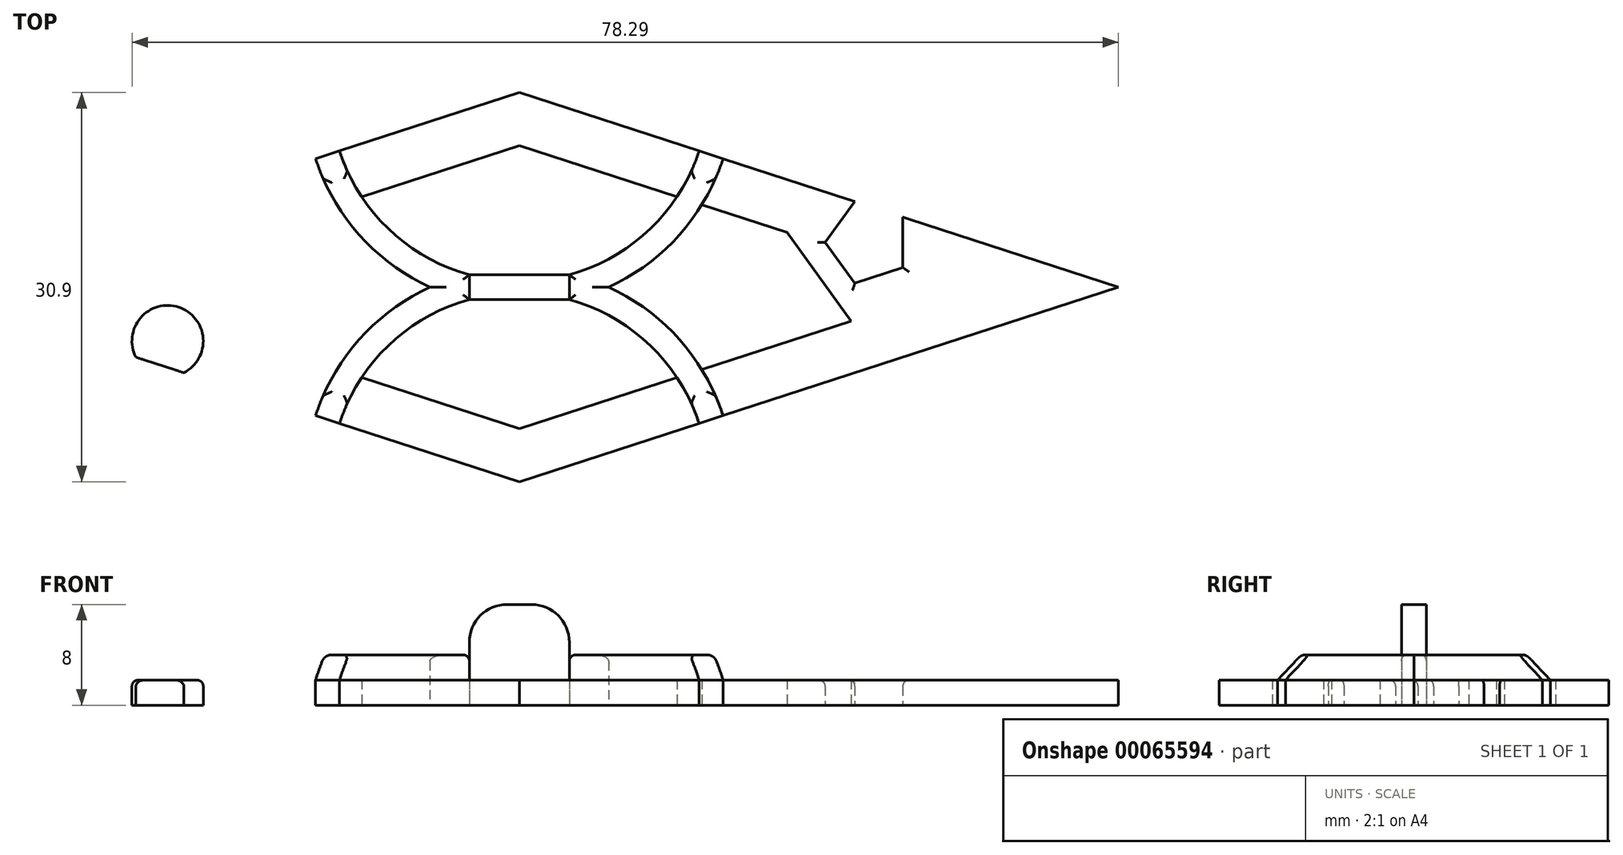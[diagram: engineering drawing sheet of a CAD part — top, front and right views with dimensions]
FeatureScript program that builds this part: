
annotation { "Feature Type Name" : "Feature", "Feature Type Description" : "" }
export const myFeature = defineFeature(function(context is Context, id is Id, definition is map)
    precondition{}
    {
        {
            var Q0;
            Q0=qCreatedBy(makeId("Top.planeOp"),FACE);
            var sketch = newSketch(context, id + "F0", { "sketchPlane" : qUnion([Q0])});
            skLineSegment(sketch, "E0", {"start": v(-47.55, 0) * mm, "end": v(0, -15.45) * mm});
            skLineSegment(sketch, "E1", {"start": v(-28.53, -6.18) * mm, "end": v(-27.91, -4.28) * mm});
            skArc(sketch, "E2", {"start": v(-30.43, -5.56) * mm, "mid": v(-27.04, -1.59) * mm, "end": v(-26.63, -6.8) * mm});
            skLineSegment(sketch, "E3.MirrorCS", {"start": v(47.55, 0) * mm, "end": v(0, -15.45) * mm});
            skLineSegment(sketch, "E4.MirrorCS", {"start": v(28.53, -6.18) * mm, "end": v(29.15, -8.08) * mm});
            skArc(sketch, "E5.MirrorCS", {"start": v(30.43, -5.56) * mm, "mid": v(30.02, -10.77) * mm, "end": v(26.63, -6.8) * mm});
            skLineSegment(sketch, "E6", {"start": v(-47.55, 0) * mm, "end": v(0, 15.45) * mm});
            skCircle(sketch, "E7.cCircle", {"center": v(-29.38, 8.8) * mm, "radius": 3.4 * mm, "construction": true});
            skLineSegment(sketch, "E7.0", {"start": v(-26.63, 6.8) * mm, "end": v(-30.43, 5.56) * mm});
            skLineSegment(sketch, "E7.1", {"start": v(-30.43, 5.56) * mm, "end": v(-32.78, 8.8) * mm});
            skLineSegment(sketch, "E7.2", {"start": v(-32.78, 8.8) * mm, "end": v(-30.43, 12.03) * mm});
            skLineSegment(sketch, "E7.3", {"start": v(-30.43, 12.03) * mm, "end": v(-26.63, 10.8) * mm});
            skLineSegment(sketch, "E7.4", {"start": v(-26.63, 10.8) * mm, "end": v(-26.63, 6.8) * mm});
            skLineSegment(sketch, "E8.MirrorCS", {"start": v(47.55, 0) * mm, "end": v(0, 15.45) * mm});
            skLineSegment(sketch, "E9.MirrorCS", {"start": v(26.63, 6.8) * mm, "end": v(30.43, 5.56) * mm});
            skLineSegment(sketch, "E10.MirrorCS", {"start": v(24.28, 3.56) * mm, "end": v(26.63, 6.8) * mm});
            skLineSegment(sketch, "E11.MirrorCS", {"start": v(26.63, 0.33) * mm, "end": v(24.28, 3.56) * mm});
            skLineSegment(sketch, "E12.MirrorCS", {"start": v(30.43, 1.56) * mm, "end": v(26.63, 0.33) * mm});
            skCircle(sketch, "E13.MirrorC", {"center": v(27.68, 3.56) * mm, "radius": 3.4 * mm, "construction": true});
            skLineSegment(sketch, "E14.MirrorCS", {"start": v(30.43, 5.56) * mm, "end": v(30.43, 1.56) * mm});
            skLineSegment(sketch, "E15.0", {"start": v(26.35, -2.68) * mm, "end": v(0, -11.25) * mm});
            skLineSegment(sketch, "E16.0", {"start": v(26.35, -2.68) * mm, "end": v(21.24, 4.34) * mm});
            skLineSegment(sketch, "E17.trimOffspring", {"start": v(21.24, 4.34) * mm, "end": v(0, 11.25) * mm});
            skLineSegment(sketch, "E18.trimOffspring", {"start": v(-22.94, -3.8) * mm, "end": v(0, -11.25) * mm});
            skLineSegment(sketch, "E19.trimOffspring", {"start": v(-27.91, 2.18) * mm, "end": v(0, 11.25) * mm});
            skArc(sketch, "E20", {"start": v(16.17, -10.2) * mm, "mid": v(0, 1.55) * mm, "end": v(-16.17, -10.2) * mm});
            skArc(sketch, "E21", {"start": v(14.27, -10.82) * mm, "mid": v(0, -0.45) * mm, "end": v(-14.27, -10.82) * mm});
            skArc(sketch, "E22.MirrorCS", {"start": v(16.17, 10.2) * mm, "mid": v(0, -1.55) * mm, "end": v(-16.17, 10.2) * mm});
            skArc(sketch, "E23.MirrorCS", {"start": v(14.27, 10.82) * mm, "mid": v(0, 0.45) * mm, "end": v(-14.27, 10.82) * mm});
            skArc(sketch, "E24", {"start": v(-22.94, -3.8) * mm, "mid": v(-24.55, -0.57) * mm, "end": v(-27.91, 0.72) * mm});
            skLineSegment(sketch, "E25.trimOffspring", {"start": v(-27.91, 0.72) * mm, "end": v(-27.91, 2.18) * mm});
            skLineSegment(sketch, "E26.rect.bottom", {"start": v(3.97, 0.99) * mm, "end": v(-3.97, 0.99) * mm});
            skLineSegment(sketch, "E26.rect.top", {"start": v(3.97, -0.99) * mm, "end": v(-3.97, -0.99) * mm});
            skLineSegment(sketch, "E26.rect.left", {"start": v(3.97, 0.99) * mm, "end": v(3.97, -0.99) * mm});
            skLineSegment(sketch, "E26.rect.right", {"start": v(-3.97, 0.99) * mm, "end": v(-3.97, -0.99) * mm});
            skPoint(sketch, "E26.rect.middle", {"position": v(0, 0) * mm});
            skSolve(sketch);
        }
        {
            var Q0;
            {var subQ13=sQuery(id+"F0.wireOp",EDGE,"E2");Q0=makeQuery(id+"F0.imprint","IMPRINT",FACE,{"disambiguationData":[TD([[makeQuery(id+"F0.imprint","IMPRINT",EDGE,{"derivedFrom":subQ13}),1.0]])]});}
            var Q1;
            {var subQ2=sQuery(id+"F0.wireOp",EDGE,"E5.MirrorCS");Q1=makeQuery(id+"F0.imprint","IMPRINT",FACE,{"disambiguationData":[TD([[makeQuery(id+"F0.imprint","IMPRINT",EDGE,{"derivedFrom":subQ2}),-1.0]])]});}
            var Q2;
            Q2=makeQuery(id+"F0.imprint","IMPRINT",FACE,{"disambiguationData":[TD([[makeQuery(id+"F0.imprint","IMPRINT",EDGE,{"derivedFrom":sQuery(id+"F0.wireOp",EDGE,"E7.0")}),-1.0]])]});
            var Q3;
            {var subQ0=sQuery(id+"F0.wireOp",EDGE,"59c43cce-ddf3-466e-a771-7dc7d053fc7f");Q3=makeQuery(id+"F0.imprint","IMPRINT",FACE,{"disambiguationData":[TD([[makeQuery(id+"F0.imprint","IMPRINT",EDGE,{"derivedFrom":subQ0}),1.0]])]});}
            var Q4;
            {var subQ6=sQuery(id+"F0.wireOp",EDGE,"E8.MirrorCS");var subQ7=sQuery(id+"F0.wireOp",EDGE,"E6");var subQ8=makeQuery(id+"F0.imprint","INTERSECT",VERTEX,{"derivedFrom":[subQ7,subQ6]});Q4=makeQuery(id+"F0.imprint","IMPRINT",FACE,{"disambiguationData":[TD([[makeQuery(id+"F0.imprint","IMPRINT",EDGE,{"disambiguationData":[TD([[subQ8,1.0]])],"derivedFrom":subQ7}),-1.0]])]});}
            var Q5;
            {var subQ1=sQuery(id+"F0.wireOp",EDGE,"E10.MirrorCS");Q5=makeQuery(id+"F0.imprint","IMPRINT",FACE,{"disambiguationData":[TD([[makeQuery(id+"F0.imprint","IMPRINT",EDGE,{"derivedFrom":subQ1}),1.0]])]});}
            var Q6;
            {var subQ5=sQuery(id+"F0.wireOp",EDGE,"E3.MirrorCS");var subQ6=sQuery(id+"F0.wireOp",EDGE,"E0");var subQ7=makeQuery(id+"F0.imprint","INTERSECT",VERTEX,{"derivedFrom":[subQ6,subQ5]});Q6=makeQuery(id+"F0.imprint","IMPRINT",FACE,{"disambiguationData":[TD([[makeQuery(id+"F0.imprint","IMPRINT",EDGE,{"disambiguationData":[TD([[subQ7,1.0]])],"derivedFrom":subQ6}),1.0]])]});}
            extrude(context, id + "F1", {"entities" : qUnion([Q0, Q1, Q2, Q3, Q4, Q5, Q6]), "depth" : 2 * mm});
        }
        {
            var Q0;
            {var subQ0=sQuery(id+"F0.wireOp",EDGE,"E20");var subQ1=sQuery(id+"F0.wireOp",EDGE,"E15.0");var subQ2=makeQuery(id+"F0.imprint","INTERSECT",VERTEX,{"derivedFrom":[subQ1,subQ0]});Q0=makeQuery(id+"F0.imprint","IMPRINT",FACE,{"disambiguationData":[TD([[makeQuery(id+"F0.imprint","IMPRINT",EDGE,{"disambiguationData":[TD([[subQ2,-1.0]])],"derivedFrom":subQ1}),-1.0]])]});}
            var Q1;
            {var subQ0=sQuery(id+"F0.wireOp",EDGE,"E20");var subQ1=sQuery(id+"F0.wireOp",EDGE,"E0");var subQ2=makeQuery(id+"F0.imprint","INTERSECT",VERTEX,{"derivedFrom":[subQ1,subQ0]});Q1=makeQuery(id+"F0.imprint","IMPRINT",FACE,{"disambiguationData":[TD([[makeQuery(id+"F0.imprint","IMPRINT",EDGE,{"disambiguationData":[TD([[subQ2,-1.0]])],"derivedFrom":subQ1}),1.0]])]});}
            var Q2;
            {var subQ0=sQuery(id+"F0.wireOp",EDGE,"E20");var subQ1=sQuery(id+"F0.wireOp",EDGE,"E3.MirrorCS");var subQ2=makeQuery(id+"F0.imprint","INTERSECT",VERTEX,{"derivedFrom":[subQ1,subQ0]});Q2=makeQuery(id+"F0.imprint","IMPRINT",FACE,{"disambiguationData":[TD([[makeQuery(id+"F0.imprint","IMPRINT",EDGE,{"disambiguationData":[TD([[subQ2,-1.0]])],"derivedFrom":subQ1}),-1.0]])]});}
            var Q3;
            {var subQ0=sQuery(id+"F0.wireOp",EDGE,"E22.MirrorCS");var subQ1=sQuery(id+"F0.wireOp",EDGE,"E8.MirrorCS");var subQ2=makeQuery(id+"F0.imprint","INTERSECT",VERTEX,{"derivedFrom":[subQ1,subQ0]});Q3=makeQuery(id+"F0.imprint","IMPRINT",FACE,{"disambiguationData":[TD([[makeQuery(id+"F0.imprint","IMPRINT",EDGE,{"disambiguationData":[TD([[subQ2,-1.0]])],"derivedFrom":subQ1}),1.0]])]});}
            var Q4;
            {var subQ0=sQuery(id+"F0.wireOp",EDGE,"E22.MirrorCS");var subQ1=sQuery(id+"F0.wireOp",EDGE,"E17.trimOffspring");var subQ2=makeQuery(id+"F0.imprint","INTERSECT",VERTEX,{"derivedFrom":[subQ1,subQ0]});Q4=makeQuery(id+"F0.imprint","IMPRINT",FACE,{"disambiguationData":[TD([[makeQuery(id+"F0.imprint","IMPRINT",EDGE,{"disambiguationData":[TD([[subQ2,-1.0]])],"derivedFrom":subQ1}),1.0]])]});}
            var Q5;
            {var subQ0=sQuery(id+"F0.wireOp",EDGE,"E22.MirrorCS");var subQ1=sQuery(id+"F0.wireOp",EDGE,"E6");var subQ2=makeQuery(id+"F0.imprint","INTERSECT",VERTEX,{"derivedFrom":[subQ1,subQ0]});Q5=makeQuery(id+"F0.imprint","IMPRINT",FACE,{"disambiguationData":[TD([[makeQuery(id+"F0.imprint","IMPRINT",EDGE,{"disambiguationData":[TD([[subQ2,-1.0]])],"derivedFrom":subQ1}),-1.0]])]});}
            var Q6;
            {var subQ0=sQuery(id+"F0.wireOp",EDGE,"ZgbBNTil-YOLx-c6fL-4Jql-8XvzCHOqNkUl");Q6=makeQuery(id+"F0.imprint","IMPRINT",FACE,{"disambiguationData":[TD([[makeQuery(id+"F0.imprint","IMPRINT",EDGE,{"derivedFrom":subQ0}),-1.0]])]});}
            var Q7;
            {var subQ0=sQuery(id+"F0.wireOp",EDGE,"E26.rect.left");Q7=makeQuery(id+"F0.imprint","IMPRINT",FACE,{"disambiguationData":[TD([[makeQuery(id+"F0.imprint","IMPRINT",EDGE,{"derivedFrom":subQ0}),1.0]])]});}
            var Q8;
            {var subQ0=sQuery(id+"F0.wireOp",EDGE,"E26.rect.right");Q8=makeQuery(id+"F0.imprint","IMPRINT",FACE,{"disambiguationData":[TD([[makeQuery(id+"F0.imprint","IMPRINT",EDGE,{"derivedFrom":subQ0}),-1.0]])]});}
            var Q9;
            {var subQ0=sQuery(id+"F0.wireOp",EDGE,"E20");var subQ1=sQuery(id+"F0.wireOp",EDGE,"E18.trimOffspring");var subQ2=makeQuery(id+"F0.imprint","INTERSECT",VERTEX,{"derivedFrom":[subQ1,subQ0]});Q9=makeQuery(id+"F0.imprint","IMPRINT",FACE,{"disambiguationData":[TD([[makeQuery(id+"F0.imprint","IMPRINT",EDGE,{"disambiguationData":[TD([[subQ2,-1.0]])],"derivedFrom":subQ1}),1.0]])]});}
            var Q10;
            {var subQ0=sQuery(id+"F0.wireOp",EDGE,"E22.MirrorCS");var subQ1=sQuery(id+"F0.wireOp",EDGE,"E19.trimOffspring");var subQ2=makeQuery(id+"F0.imprint","INTERSECT",VERTEX,{"derivedFrom":[subQ1,subQ0]});Q10=makeQuery(id+"F0.imprint","IMPRINT",FACE,{"disambiguationData":[TD([[makeQuery(id+"F0.imprint","IMPRINT",EDGE,{"disambiguationData":[TD([[subQ2,-1.0]])],"derivedFrom":subQ1}),-1.0]])]});}
            extrude(context, id + "F2", {"entities" : qUnion([Q0, Q1, Q2, Q3, Q4, Q5, Q6, Q7, Q8, Q9, Q10]), "depth" : 4 * mm});
        }
        {
            var Q0;
            Q0=makeQuery(id+"F2.opExtrude","CAP_EDGE",EDGE,{"disambiguationData":[OSD([sQuery(id+"F0.wireOp",EDGE,"E0")])],"isStart":false});
            var Q1;
            Q1=makeQuery(id+"F2.opExtrude","CAP_EDGE",EDGE,{"disambiguationData":[OSD([sQuery(id+"F0.wireOp",EDGE,"E3.MirrorCS")])],"isStart":false});
            var Q2;
            Q2=makeQuery(id+"F2.opExtrude","CAP_EDGE",EDGE,{"disambiguationData":[OSD([sQuery(id+"F0.wireOp",EDGE,"E8.MirrorCS")])],"isStart":false});
            var Q3;
            Q3=makeQuery(id+"F2.opExtrude","CAP_EDGE",EDGE,{"disambiguationData":[OSD([sQuery(id+"F0.wireOp",EDGE,"E6")])],"isStart":false});
            chamfer(context, id + "F3", {"entities" : qUnion([Q0, Q1, Q2, Q3]), "chamferType" : ChamferType.TWO_OFFSETS, "width1" : 2 * mm, "oppositeDirection" : false, "width2" : 2 * mm, "tangentPropagation" : true});
        }
        {
            var Q0;
            Q0=makeQuery(id+"F1.opExtrude","CAP_EDGE",EDGE,{"disambiguationData":[OSD([sQuery(id+"F0.wireOp",EDGE,"E2")])],"isStart":false});
            var Q1;
            Q1=makeQuery(id+"F1.opExtrude","CAP_EDGE",EDGE,{"disambiguationData":[OSD([sQuery(id+"F0.wireOp",EDGE,"E10.MirrorCS")])],"isStart":false});
            var Q2;
            Q2=makeQuery(id+"F1.opExtrude","CAP_EDGE",EDGE,{"disambiguationData":[OSD([sQuery(id+"F0.wireOp",EDGE,"E11.MirrorCS")])],"isStart":false});
            var Q3;
            Q3=makeQuery(id+"F1.opExtrude","CAP_EDGE",EDGE,{"disambiguationData":[OSD([sQuery(id+"F0.wireOp",EDGE,"E12.MirrorCS")])],"isStart":false});
            var Q4;
            Q4=makeQuery(id+"F1.opExtrude","CAP_EDGE",EDGE,{"disambiguationData":[OSD([sQuery(id+"F0.wireOp",EDGE,"E14.MirrorCS")])],"isStart":false});
            var Q5;
            Q5=makeQuery(id+"F2.opExtrude","CAP_EDGE",EDGE,{"disambiguationData":[OSD([sQuery(id+"F0.wireOp",EDGE,"E21")])],"isStart":false});
            var Q6;
            Q6=makeQuery(id+"F2.opExtrude","CAP_EDGE",EDGE,{"disambiguationData":[OSD([sQuery(id+"F0.wireOp",EDGE,"E20")])],"isStart":false});
            var Q7;
            {var subQ0=sQuery(id+"F0.wireOp",EDGE,"E0");Q7=makeQuery(id+"F3.opChamfer","BLEND_EDGE",EDGE,{"blendedFrom":[makeQuery(id+"F2.opExtrude","CAP_EDGE",EDGE,{"disambiguationData":[OSD([subQ0])],"isStart":false}),makeQuery(id+"F2.opExtrude","CAP_FACE",FACE,{"disambiguationData":[OSD([subQ0,sQuery(id+"F0.wireOp",EDGE,"E3.MirrorCS"),sQuery(id+"F0.wireOp",EDGE,"E20"),sQuery(id+"F0.wireOp",EDGE,"E21")])],"isStart":false})],"blendedInto":[makeQuery(id+"F2.opExtrude","CAP_FACE",FACE,{"disambiguationData":[OSD([subQ0,sQuery(id+"F0.wireOp",EDGE,"E3.MirrorCS"),sQuery(id+"F0.wireOp",EDGE,"E20"),sQuery(id+"F0.wireOp",EDGE,"E21")])],"isStart":false})]});}
            var Q8;
            {var subQ0=sQuery(id+"F0.wireOp",EDGE,"E3.MirrorCS");Q8=makeQuery(id+"F3.opChamfer","BLEND_EDGE",EDGE,{"blendedFrom":[makeQuery(id+"F2.opExtrude","CAP_EDGE",EDGE,{"disambiguationData":[OSD([subQ0])],"isStart":false}),makeQuery(id+"F2.opExtrude","CAP_FACE",FACE,{"disambiguationData":[OSD([sQuery(id+"F0.wireOp",EDGE,"E0"),subQ0,sQuery(id+"F0.wireOp",EDGE,"E20"),sQuery(id+"F0.wireOp",EDGE,"E21")])],"isStart":false})],"blendedInto":[makeQuery(id+"F2.opExtrude","CAP_FACE",FACE,{"disambiguationData":[OSD([sQuery(id+"F0.wireOp",EDGE,"E0"),subQ0,sQuery(id+"F0.wireOp",EDGE,"E20"),sQuery(id+"F0.wireOp",EDGE,"E21")])],"isStart":false})]});}
            var Q9;
            Q9=makeQuery(id+"F2.opExtrude","CAP_EDGE",EDGE,{"disambiguationData":[OSD([sQuery(id+"F0.wireOp",EDGE,"E22.MirrorCS")])],"isStart":false});
            var Q10;
            Q10=makeQuery(id+"F2.opExtrude","CAP_EDGE",EDGE,{"disambiguationData":[OSD([sQuery(id+"F0.wireOp",EDGE,"E23.MirrorCS")])],"isStart":false});
            var Q11;
            {var subQ0=sQuery(id+"F0.wireOp",EDGE,"E8.MirrorCS");Q11=makeQuery(id+"F3.opChamfer","BLEND_EDGE",EDGE,{"blendedFrom":[makeQuery(id+"F2.opExtrude","CAP_EDGE",EDGE,{"disambiguationData":[OSD([subQ0])],"isStart":false}),makeQuery(id+"F2.opExtrude","CAP_FACE",FACE,{"disambiguationData":[OSD([sQuery(id+"F0.wireOp",EDGE,"E6"),subQ0,sQuery(id+"F0.wireOp",EDGE,"E22.MirrorCS"),sQuery(id+"F0.wireOp",EDGE,"E23.MirrorCS")])],"isStart":false})],"blendedInto":[makeQuery(id+"F2.opExtrude","CAP_FACE",FACE,{"disambiguationData":[OSD([sQuery(id+"F0.wireOp",EDGE,"E6"),subQ0,sQuery(id+"F0.wireOp",EDGE,"E22.MirrorCS"),sQuery(id+"F0.wireOp",EDGE,"E23.MirrorCS")])],"isStart":false})]});}
            var Q12;
            {var subQ0=sQuery(id+"F0.wireOp",EDGE,"E6");Q12=makeQuery(id+"F3.opChamfer","BLEND_EDGE",EDGE,{"blendedFrom":[makeQuery(id+"F2.opExtrude","CAP_EDGE",EDGE,{"disambiguationData":[OSD([subQ0])],"isStart":false}),makeQuery(id+"F2.opExtrude","CAP_FACE",FACE,{"disambiguationData":[OSD([subQ0,sQuery(id+"F0.wireOp",EDGE,"E8.MirrorCS"),sQuery(id+"F0.wireOp",EDGE,"E22.MirrorCS"),sQuery(id+"F0.wireOp",EDGE,"E23.MirrorCS")])],"isStart":false})],"blendedInto":[makeQuery(id+"F2.opExtrude","CAP_FACE",FACE,{"disambiguationData":[OSD([subQ0,sQuery(id+"F0.wireOp",EDGE,"E8.MirrorCS"),sQuery(id+"F0.wireOp",EDGE,"E22.MirrorCS"),sQuery(id+"F0.wireOp",EDGE,"E23.MirrorCS")])],"isStart":false})]});}
            var Q13;
            Q13=makeQuery(id+"F2.opExtrude","CAP_EDGE",EDGE,{"disambiguationData":[OSD([sQuery(id+"F0.wireOp",EDGE,"ZgbBNTil-YOLx-c6fL-4Jql-8XvzCHOqNkUl")])],"isStart":false});
            var Q14;
            Q14=makeQuery(id+"F2.opExtrude","CAP_FACE",FACE,{"disambiguationData":[OSD([sQuery(id+"F0.wireOp",EDGE,"E0"),sQuery(id+"F0.wireOp",EDGE,"E3.MirrorCS"),sQuery(id+"F0.wireOp",EDGE,"E6"),sQuery(id+"F0.wireOp",EDGE,"E8.MirrorCS"),sQuery(id+"F0.wireOp",EDGE,"E20"),sQuery(id+"F0.wireOp",EDGE,"E21"),sQuery(id+"F0.wireOp",EDGE,"E22.MirrorCS"),sQuery(id+"F0.wireOp",EDGE,"E23.MirrorCS"),sQuery(id+"F0.wireOp",EDGE,"ZgbBNTil-YOLx-c6fL-4Jql-8XvzCHOqNkUl"),sQuery(id+"F0.wireOp",EDGE,"812214a2-db5b-4d45-a7c5-42e99ade8bce0.MirrorCS")])],"isStart":false});
            fillet(context, id + "F4", {"entities" : qUnion([Q0, Q1, Q2, Q3, Q4, Q5, Q6, Q7, Q8, Q9, Q10, Q11, Q12, Q13, Q14]), "radius" : 0.5 * mm, "tangentPropagation" : true, "allowEdgeOverflow" : false});
        }
        {
            var Q0;
            {var subQ0=sQuery(id+"F0.wireOp",EDGE,"E26.rect.left");Q0=makeQuery(id+"F0.imprint","IMPRINT",FACE,{"disambiguationData":[TD([[makeQuery(id+"F0.imprint","IMPRINT",EDGE,{"derivedFrom":subQ0}),-1.0]])]});}
            var Q1;
            {var subQ0=sQuery(id+"F0.wireOp",EDGE,"E26.rect.top");Q1=makeQuery(id+"F0.imprint","IMPRINT",FACE,{"disambiguationData":[TD([[makeQuery(id+"F0.imprint","IMPRINT",EDGE,{"derivedFrom":subQ0}),-1.0]])]});}
            var Q2;
            {var subQ0=sQuery(id+"F0.wireOp",EDGE,"E26.rect.bottom");Q2=makeQuery(id+"F0.imprint","IMPRINT",FACE,{"disambiguationData":[TD([[makeQuery(id+"F0.imprint","IMPRINT",EDGE,{"derivedFrom":subQ0}),1.0]])]});}
            extrude(context, id + "F5", {"entities" : qUnion([Q0, Q1, Q2]), "depth" : 8 * mm});
        }
        {
            var Q0;
            Q0=makeQuery(id+"F5.opExtrude","CAP_EDGE",EDGE,{"disambiguationData":[OSD([sQuery(id+"F0.wireOp",EDGE,"E26.rect.left")])],"isStart":false});
            var Q1;
            Q1=makeQuery(id+"F5.opExtrude","CAP_EDGE",EDGE,{"disambiguationData":[OSD([sQuery(id+"F0.wireOp",EDGE,"E26.rect.right")])],"isStart":false});
            fillet(context, id + "F6", {"entities" : qUnion([Q0, Q1]), "radius" : 3 * mm, "tangentPropagation" : true, "allowEdgeOverflow" : false});
        }
    });
